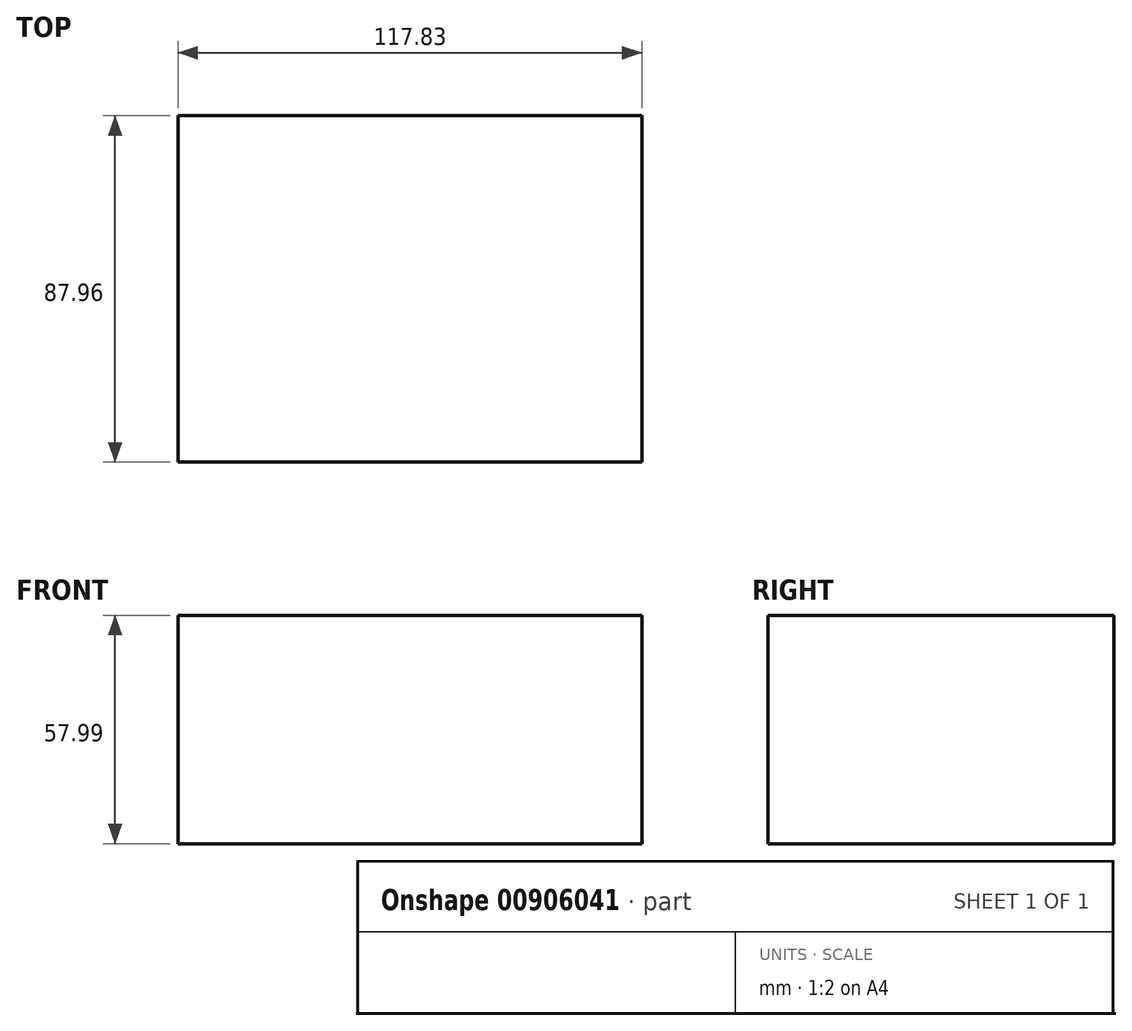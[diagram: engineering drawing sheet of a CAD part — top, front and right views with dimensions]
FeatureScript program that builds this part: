
annotation { "Feature Type Name" : "Feature", "Feature Type Description" : "" }
export const myFeature = defineFeature(function(context is Context, id is Id, definition is map)
    precondition{}
    {
        {
            var Q0;
            Q0=qCreatedBy(makeId("Front.planeOp"),FACE);
            var sketch = newSketch(context, id + "F0", { "sketchPlane" : qUnion([Q0])});
            skLineSegment(sketch, "E0.bottom", {"start": v(-88.62, 12.8) * mm, "end": v(29.2, 12.8) * mm});
            skLineSegment(sketch, "E0.top", {"start": v(-88.62, -45.2) * mm, "end": v(29.2, -45.2) * mm});
            skLineSegment(sketch, "E0.left", {"start": v(-88.62, 12.8) * mm, "end": v(-88.62, -45.2) * mm});
            skLineSegment(sketch, "E0.right", {"start": v(29.2, 12.8) * mm, "end": v(29.2, -45.2) * mm});
            skSolve(sketch);
        }
        {
            var Q0;
            Q0=makeQuery(id+"F0.imprint","IMPRINT",FACE,{"disambiguationData":[TD([[makeQuery(id+"F0.imprint","IMPRINT",EDGE,{"derivedFrom":sQuery(id+"F0.wireOp",EDGE,"E0.bottom")}),-1.0]])]});
            extrude(context, id + "F1", {"entities" : qUnion([Q0]), "depth" : 87.96 * mm, "offsetDistance" : 25.4 * mm});
        }
    });
